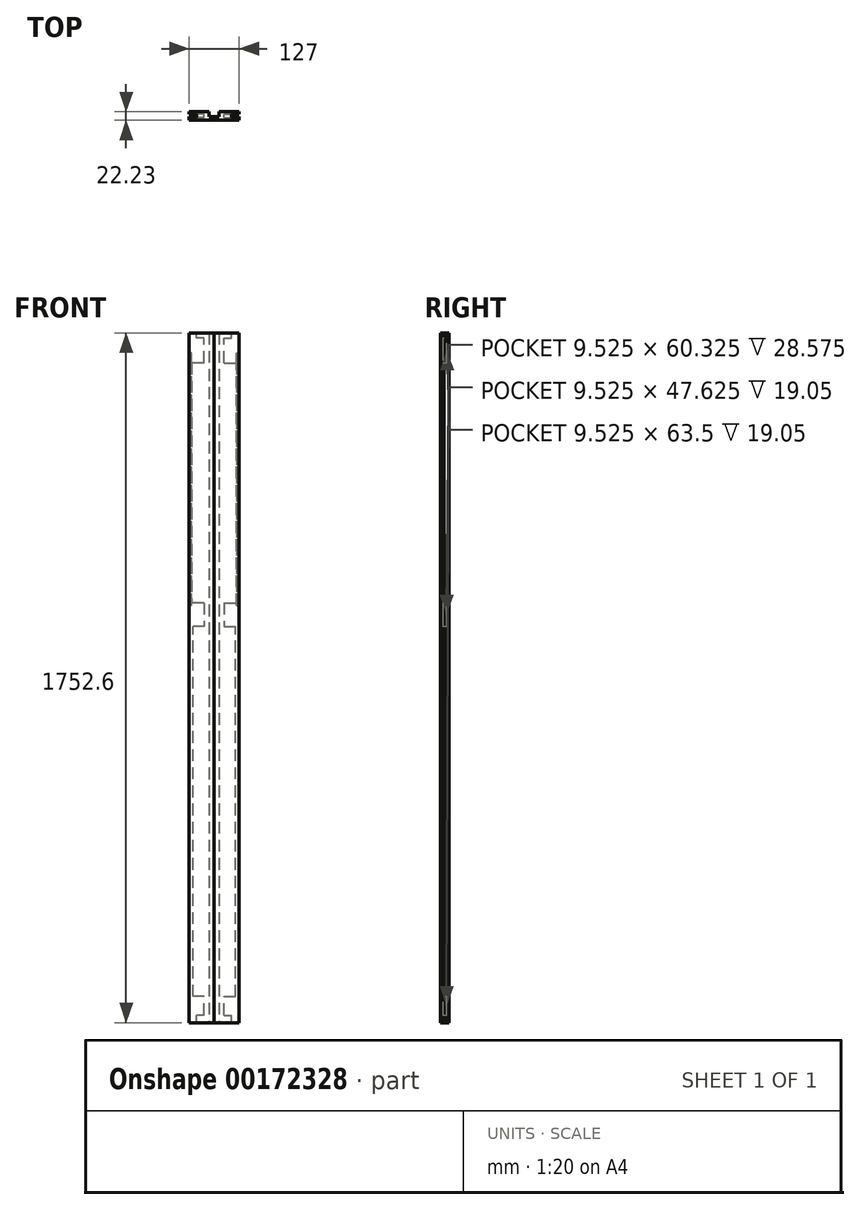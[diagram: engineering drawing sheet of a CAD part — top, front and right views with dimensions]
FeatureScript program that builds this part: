
annotation { "Feature Type Name" : "Feature", "Feature Type Description" : "" }
export const myFeature = defineFeature(function(context is Context, id is Id, definition is map)
    precondition{}
    {
        {
            var Q0;
            Q0=qCreatedBy(makeId("Front.planeOp"),FACE);
            var sketch = newSketch(context, id + "F0", { "sketchPlane" : qUnion([Q0])});
            skLineSegment(sketch, "E0.bottom", {"start": v(0, 0) * mm, "end": v(-63.5, 0) * mm});
            skLineSegment(sketch, "E0.top", {"start": v(0, 1778) * mm, "end": v(-63.5, 1778) * mm});
            skLineSegment(sketch, "E0.left", {"start": v(0, 0) * mm, "end": v(0, 1778) * mm});
            skLineSegment(sketch, "E0.right", {"start": v(-63.5, 0) * mm, "end": v(-63.5, 1778) * mm});
            skSolve(sketch);
        }
        {
            var Q0;
            Q0=makeQuery(id+"F0.imprint","IMPRINT",FACE,{"disambiguationData":[TD([[makeQuery(id+"F0.imprint","IMPRINT",EDGE,{"derivedFrom":sQuery(id+"F0.wireOp",EDGE,"E0.bottom")}),-1.0]])]});
            extrude(context, id + "F1", {"entities" : qUnion([Q0]), "depth" : 22.22 * mm});
        }
        {
            var Q0;
            Q0=makeQuery(id+"F1.opExtrude","SWEPT_FACE",FACE,{"disambiguationData":[OSD([sQuery(id+"F0.wireOp",EDGE,"E0.right")])]});
            var sketch = newSketch(context, id + "F2", { "sketchPlane" : qUnion([Q0])});
            skLineSegment(sketch, "E1.bottom", {"start": v(6.35, 0) * mm, "end": v(15.88, 0) * mm});
            skLineSegment(sketch, "E1.top", {"start": v(6.35, 79.38) * mm, "end": v(15.88, 79.38) * mm});
            skLineSegment(sketch, "E1.left", {"start": v(6.35, 0) * mm, "end": v(6.35, 79.37) * mm});
            skLineSegment(sketch, "E1.right", {"start": v(15.88, 0) * mm, "end": v(15.88, 79.37) * mm});
            skLineSegment(sketch, "E2.bottom", {"start": v(15.87, 1689.1) * mm, "end": v(6.35, 1689.1) * mm});
            skLineSegment(sketch, "E2.top", {"start": v(15.87, 1778) * mm, "end": v(6.35, 1778) * mm});
            skLineSegment(sketch, "E2.left", {"start": v(15.87, 1689.1) * mm, "end": v(15.87, 1778) * mm});
            skLineSegment(sketch, "E2.right", {"start": v(6.35, 1689.1) * mm, "end": v(6.35, 1778) * mm});
            skLineSegment(sketch, "E3", {"start": v(6.35, 31.75) * mm, "end": v(15.88, 31.75) * mm});
            skLineSegment(sketch, "E4", {"start": v(6.35, 1752.6) * mm, "end": v(15.87, 1752.6) * mm});
            skLineSegment(sketch, "E5.bottom", {"start": v(15.88, 1079.5) * mm, "end": v(6.35, 1079.5) * mm});
            skLineSegment(sketch, "E5.top", {"start": v(15.87, 1019.18) * mm, "end": v(6.35, 1019.18) * mm});
            skLineSegment(sketch, "E5.left", {"start": v(15.87, 1079.5) * mm, "end": v(15.87, 1019.18) * mm});
            skLineSegment(sketch, "E5.right", {"start": v(6.35, 1079.5) * mm, "end": v(6.35, 1019.18) * mm});
            skLineSegment(sketch, "E6.bottom", {"start": v(0, 1104.9) * mm, "end": v(22.22, 1104.9) * mm, "construction": true});
            skLineSegment(sketch, "E6.top", {"start": v(0, 993.78) * mm, "end": v(22.23, 993.78) * mm, "construction": true});
            skLineSegment(sketch, "E6.left", {"start": v(0, 993.78) * mm, "end": v(0, 1104.9) * mm, "construction": true});
            skLineSegment(sketch, "E6.right", {"start": v(22.22, 993.78) * mm, "end": v(22.22, 1104.9) * mm, "construction": true});
            skSolve(sketch);
        }
        {
            var Q0;
            {var subQ0=sQuery(id+"F2.wireOp",EDGE,"E2.bottom");Q0=makeQuery(id+"F2.imprint","IMPRINT",FACE,{"disambiguationData":[TD([[makeQuery(id+"F2.imprint","IMPRINT",EDGE,{"derivedFrom":subQ0}),-1.0]])]});}
            var Q1;
            {var subQ0=sQuery(id+"F2.wireOp",EDGE,"E1.top");Q1=makeQuery(id+"F2.imprint","IMPRINT",FACE,{"disambiguationData":[TD([[makeQuery(id+"F2.imprint","IMPRINT",EDGE,{"derivedFrom":subQ0}),-1.0]])]});}
            var Q2;
            Q2=makeQuery(id+"F2.imprint","IMPRINT",FACE,{"disambiguationData":[TD([[makeQuery(id+"F2.imprint","IMPRINT",EDGE,{"derivedFrom":sQuery(id+"F2.wireOp",EDGE,"E5.bottom")}),1.0]])]});
            extrude(context, id + "F3", {"entities" : qUnion([Q0, Q1, Q2]), "operationType" : NewBodyOperationType.REMOVE, "oppositeDirection" : true, "depth" : 38.1 * mm});
        }
        {
            var Q0;
            {var subQ0=sQuery(id+"F2.wireOp",EDGE,"E2.top");Q0=makeQuery(id+"F2.imprint","IMPRINT",FACE,{"disambiguationData":[TD([[makeQuery(id+"F2.imprint","IMPRINT",EDGE,{"derivedFrom":subQ0}),1.0]])]});}
            var Q1;
            {var subQ0=sQuery(id+"F2.wireOp",EDGE,"E1.bottom");Q1=makeQuery(id+"F2.imprint","IMPRINT",FACE,{"disambiguationData":[TD([[makeQuery(id+"F2.imprint","IMPRINT",EDGE,{"derivedFrom":subQ0}),-1.0]])]});}
            extrude(context, id + "F4", {"entities" : qUnion([Q0, Q1]), "operationType" : NewBodyOperationType.REMOVE, "oppositeDirection" : true, "depth" : 19.05 * mm});
        }
        {
            var Q0;
            Q0=qCreatedBy(makeId("Top.planeOp"),FACE);
            var sketch = newSketch(context, id + "F5", { "sketchPlane" : qUnion([Q0])});
            skLineSegment(sketch, "E7.bottom", {"start": v(-12.7, 0) * mm, "end": v(0, 0) * mm});
            skLineSegment(sketch, "E7.top", {"start": v(-12.7, -12.7) * mm, "end": v(0, -12.7) * mm});
            skLineSegment(sketch, "E7.left", {"start": v(-12.7, 0) * mm, "end": v(-12.7, -12.7) * mm});
            skLineSegment(sketch, "E7.right", {"start": v(0, 0) * mm, "end": v(0, -12.7) * mm});
            skSolve(sketch);
        }
        {
            var Q0;
            Q0=makeQuery(id+"F5.imprint","IMPRINT",FACE,{"disambiguationData":[TD([[makeQuery(id+"F5.imprint","IMPRINT",EDGE,{"derivedFrom":sQuery(id+"F5.wireOp",EDGE,"E7.bottom")}),-1.0]])]});
            extrude(context, id + "F6", {"entities" : qUnion([Q0]), "operationType" : NewBodyOperationType.REMOVE, "endBound" : BoundingType.UP_TO_NEXT, "depth" : 25.4 * mm});
        }
        {
            var Q0;
            Q0=makeQuery(id+"F1.opExtrude","CAP_FACE",FACE,{"disambiguationData":[OSD([sQuery(id+"F0.wireOp",EDGE,"E0.bottom"),sQuery(id+"F0.wireOp",EDGE,"E0.top"),sQuery(id+"F0.wireOp",EDGE,"E0.left"),sQuery(id+"F0.wireOp",EDGE,"E0.right")])],"isStart":false});
            var sketch = newSketch(context, id + "F7", { "sketchPlane" : qUnion([Q0])});
            skLineSegment(sketch, "E8", {"start": v(-63.5, 12.7) * mm, "end": v(0, 12.7) * mm});
            skLineSegment(sketch, "E9", {"start": v(-63.5, 1765.3) * mm, "end": v(0, 1765.3) * mm});
            skSolve(sketch);
        }
        {
            var Q0;
            Q0=qSketchRegion(id+"F7",true);
            var Q1;
            {var subQ0=sQuery(id+"F7.wireOp",EDGE,"E9");Q1=makeQuery(id+"F7.imprint","IMPRINT",FACE,{"disambiguationData":[TD([[makeQuery(id+"F7.imprint","IMPRINT",EDGE,{"derivedFrom":subQ0}),1.0]])]});}
            var Q2;
            {var subQ0=sQuery(id+"F7.wireOp",EDGE,"E8");Q2=makeQuery(id+"F7.imprint","IMPRINT",FACE,{"disambiguationData":[TD([[makeQuery(id+"F7.imprint","IMPRINT",EDGE,{"derivedFrom":subQ0}),-1.0]])]});}
            extrude(context, id + "F8", {"entities" : qUnion([Q0, Q1, Q2]), "operationType" : NewBodyOperationType.REMOVE, "endBound" : BoundingType.THROUGH_ALL, "oppositeDirection" : true, "depth" : 25.4 * mm});
        }
        {
            var Q0;
            Q0=makeQuery(id+"F1.opExtrude","SWEPT_FACE",FACE,{"disambiguationData":[OSD([sQuery(id+"F0.wireOp",EDGE,"E0.right")])]});
            var sketch = newSketch(context, id + "F9", { "sketchPlane" : qUnion([Q0])});
            skLineSegment(sketch, "E10.bottom", {"start": v(15.88, 79.37) * mm, "end": v(6.35, 79.37) * mm});
            skLineSegment(sketch, "E10.top", {"start": v(15.87, 1019.18) * mm, "end": v(6.35, 1019.18) * mm});
            skLineSegment(sketch, "E10.left", {"start": v(15.88, 79.37) * mm, "end": v(15.87, 1019.18) * mm});
            skLineSegment(sketch, "E10.right", {"start": v(6.35, 79.37) * mm, "end": v(6.35, 1019.18) * mm});
            skSolve(sketch);
        }
        {
            var Q0;
            {var subQ0=sQuery(id+"F9.wireOp",EDGE,"E10.top");Q0=makeQuery(id+"F9.imprint","IMPRINT",FACE,{"disambiguationData":[TD([[makeQuery(id+"F9.imprint","IMPRINT",EDGE,{"derivedFrom":subQ0}),1.0]])]});}
            var Q1;
            {var subQ0=sQuery(id+"F9.wireOp",EDGE,"E10.bottom");Q1=makeQuery(id+"F9.imprint","IMPRINT",FACE,{"disambiguationData":[TD([[makeQuery(id+"F9.imprint","IMPRINT",EDGE,{"derivedFrom":subQ0}),1.0]])]});}
            extrude(context, id + "F10", {"entities" : qUnion([Q0, Q1]), "operationType" : NewBodyOperationType.REMOVE, "oppositeDirection" : true, "depth" : 9.52 * mm});
        }
        {
            var Q0;
            Q0=makeQuery(id+"F1.opExtrude","SWEPT_FACE",FACE,{"disambiguationData":[OSD([sQuery(id+"F0.wireOp",EDGE,"E0.right")])]});
            var sketch = newSketch(context, id + "F11", { "sketchPlane" : qUnion([Q0])});
            skLineSegment(sketch, "E11.bottom", {"start": v(0, 1714.5) * mm, "end": v(12.7, 1714.5) * mm});
            skLineSegment(sketch, "E11.top", {"start": v(0, 1073.15) * mm, "end": v(12.7, 1073.15) * mm});
            skLineSegment(sketch, "E11.left", {"start": v(0, 1714.5) * mm, "end": v(0, 1073.15) * mm});
            skLineSegment(sketch, "E11.right", {"start": v(12.7, 1714.5) * mm, "end": v(12.7, 1073.15) * mm});
            skSolve(sketch);
        }
        {
            var Q0;
            {var subQ5=sQuery(id+"F11.wireOp",EDGE,"E11.left");Q0=makeQuery(id+"F11.imprint","IMPRINT",FACE,{"disambiguationData":[TD([[makeQuery(id+"F11.imprint","IMPRINT",EDGE,{"derivedFrom":subQ5}),-1.0]])]});}
            extrude(context, id + "F12", {"entities" : qUnion([Q0]), "operationType" : NewBodyOperationType.REMOVE, "oppositeDirection" : true, "depth" : 6.35 * mm});
        }
        {
            var Q0;
            Q0=makeQuery(id+"F1.opExtrude","SWEPT_BODY",BODY,{"disambiguationData":[OSD([sQuery(id+"F0.wireOp",EDGE,"E0.bottom"),sQuery(id+"F0.wireOp",EDGE,"E0.top"),sQuery(id+"F0.wireOp",EDGE,"E0.left"),sQuery(id+"F0.wireOp",EDGE,"E0.right")])]});
            var Q1;
            Q1=qCreatedBy(makeId("Right.planeOp"),FACE);
            mirror(context, id + "F13", {"entities" : qUnion([Q0]), "mirrorPlane" : qUnion([Q1])});
        }
    });
